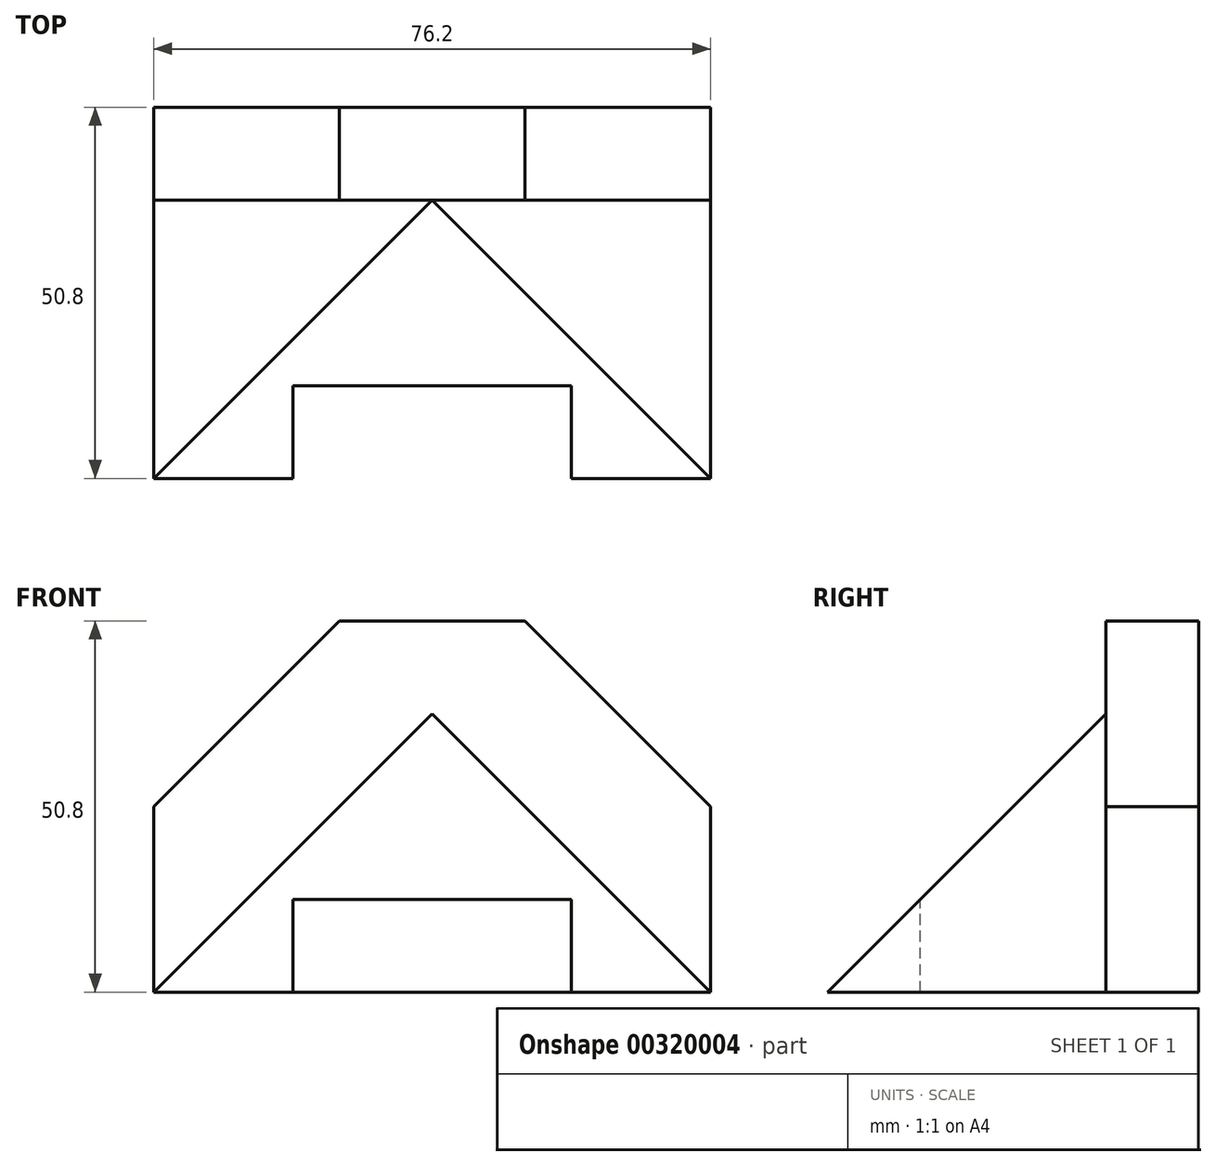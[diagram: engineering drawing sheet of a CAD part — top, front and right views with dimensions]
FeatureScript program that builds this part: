
annotation { "Feature Type Name" : "Feature", "Feature Type Description" : "" }
export const myFeature = defineFeature(function(context is Context, id is Id, definition is map)
    precondition{}
    {
        {
            var Q0;
            Q0=qCreatedBy(makeId("Front.planeOp"),FACE);
            var sketch = newSketch(context, id + "F0", { "sketchPlane" : qUnion([Q0])});
            skLineSegment(sketch, "E0.bottom", {"start": v(0, 0) * mm, "end": v(76.2, 0) * mm});
            skLineSegment(sketch, "E0.top", {"start": v(0, 50.8) * mm, "end": v(76.2, 50.8) * mm});
            skLineSegment(sketch, "E0.left", {"start": v(0, 0) * mm, "end": v(0, 50.8) * mm});
            skLineSegment(sketch, "E0.right", {"start": v(76.2, 0) * mm, "end": v(76.2, 50.8) * mm});
            skSolve(sketch);
        }
        {
            var Q0;
            Q0 = qSketchRegion(id + "F0", true);
            extrude(context, id + "F1", {"entities" : qUnion([Q0]), "oppositeDirection" : true, "depth" : 50.8 * mm});
        }
        {
            var Q0;
            Q0=makeQuery(id+"F1.opExtrude","CAP_FACE",FACE,{"disambiguationData":[OSD([sQuery(id+"F0.wireOp",EDGE,"E0.bottom"),sQuery(id+"F0.wireOp",EDGE,"E0.top"),sQuery(id+"F0.wireOp",EDGE,"E0.left"),sQuery(id+"F0.wireOp",EDGE,"E0.right")])],"isStart":true});
            var sketch = newSketch(context, id + "F2", { "sketchPlane" : qUnion([Q0])});
            skLineSegment(sketch, "E1.bottom", {"start": v(19.05, 0) * mm, "end": v(57.15, 0) * mm});
            skLineSegment(sketch, "E1.top", {"start": v(19.05, 12.7) * mm, "end": v(57.15, 12.7) * mm});
            skLineSegment(sketch, "E1.left", {"start": v(19.05, 0) * mm, "end": v(19.05, 12.7) * mm});
            skLineSegment(sketch, "E1.right", {"start": v(57.15, 0) * mm, "end": v(57.15, 12.7) * mm});
            skPoint(sketch, "E2.start.orphan", {"position": v(38.1, 0) * mm});
            skSolve(sketch);
        }
        {
            var Q0;
            Q0 = qSketchRegion(id + "F2", true);
            extrude(context, id + "F3", {"entities" : qUnion([Q0]), "operationType" : NewBodyOperationType.REMOVE, "oppositeDirection" : true, "depth" : 12.7 * mm});
        }
        {
            var Q0;
            Q0=makeQuery(id+"F1.opExtrude","SWEPT_FACE",FACE,{"disambiguationData":[OSD([sQuery(id+"F0.wireOp",EDGE,"E0.right")])]});
            var sketch = newSketch(context, id + "F4", { "sketchPlane" : qUnion([Q0])});
            skLineSegment(sketch, "E3", {"start": v(0, 0) * mm, "end": v(0, 50.8) * mm});
            skLineSegment(sketch, "E4", {"start": v(0, 50.8) * mm, "end": v(38.1, 50.8) * mm});
            skLineSegment(sketch, "E5", {"start": v(38.1, 50.8) * mm, "end": v(38.1, 38.1) * mm});
            skLineSegment(sketch, "E6", {"start": v(38.1, 38.1) * mm, "end": v(0, 0) * mm});
            skSolve(sketch);
        }
        {
            var Q0;
            Q0 = qSketchRegion(id + "F4", true);
            extrude(context, id + "F5", {"entities" : qUnion([Q0]), "operationType" : NewBodyOperationType.REMOVE, "endBound" : BoundingType.THROUGH_ALL, "oppositeDirection" : true, "depth" : 25.4 * mm});
        }
        {
            var Q0;
            Q0=makeQuery(id+"F1.opExtrude","CAP_FACE",FACE,{"disambiguationData":[OSD([sQuery(id+"F0.wireOp",EDGE,"E0.bottom"),sQuery(id+"F0.wireOp",EDGE,"E0.top"),sQuery(id+"F0.wireOp",EDGE,"E0.left"),sQuery(id+"F0.wireOp",EDGE,"E0.right")])],"isStart":false});
            var sketch = newSketch(context, id + "F6", { "sketchPlane" : qUnion([Q0])});
            skLineSegment(sketch, "E7", {"start": v(-25.4, 50.8) * mm, "end": v(0, 50.8) * mm});
            skLineSegment(sketch, "E8", {"start": v(0, 50.8) * mm, "end": v(0, 25.4) * mm});
            skLineSegment(sketch, "E9", {"start": v(0, 25.4) * mm, "end": v(-25.4, 50.8) * mm});
            skLineSegment(sketch, "E10", {"start": v(-50.8, 50.8) * mm, "end": v(-76.2, 50.8) * mm});
            skLineSegment(sketch, "E11", {"start": v(-76.2, 50.8) * mm, "end": v(-76.2, 25.4) * mm});
            skLineSegment(sketch, "E12", {"start": v(-76.2, 25.4) * mm, "end": v(-50.8, 50.8) * mm});
            skSolve(sketch);
        }
        {
            var Q0;
            Q0 = qSketchRegion(id + "F6", true);
            extrude(context, id + "F7", {"entities" : qUnion([Q0]), "operationType" : NewBodyOperationType.REMOVE, "endBound" : BoundingType.THROUGH_ALL, "oppositeDirection" : true, "depth" : 25.4 * mm});
        }
        {
            var Q0;
            Q0=qCreatedBy(makeId("Front.planeOp"),FACE);
            cPlane(context, id + "F8", {"entities" : qUnion([Q0]), "cplaneType" : CPlaneType.OFFSET, "offset" : 38.1 * mm, "oppositeDirection" : true, "width" : 152.4 * mm, "height" : 152.4 * mm});
        }
        {
            var Q0;
            Q0=qCreatedBy(id+"F8.planeOp",FACE);
            var sketch = newSketch(context, id + "F9", { "sketchPlane" : qUnion([Q0])});
            skLineSegment(sketch, "E13.0", {"start": v(12.7, 38.1) * mm, "end": v(63.5, 38.1) * mm});
            skPoint(sketch, "E14.0", {"position": v(76.2, 0) * mm});
            skPoint(sketch, "E15.0", {"position": v(0, 0) * mm});
            skLineSegment(sketch, "E16", {"start": v(38.1, 38.1) * mm, "end": v(76.2, 0) * mm});
            skLineSegment(sketch, "E17.0", {"start": v(63.5, 38.1) * mm, "end": v(76.2, 25.4) * mm});
            skLineSegment(sketch, "E18.0", {"start": v(76.2, 25.4) * mm, "end": v(76.2, 0) * mm});
            skLineSegment(sketch, "E19.0", {"start": v(12.7, 38.1) * mm, "end": v(0, 25.4) * mm});
            skLineSegment(sketch, "E20.0", {"start": v(0, 25.4) * mm, "end": v(0, 0) * mm});
            skLineSegment(sketch, "E21", {"start": v(38.1, 38.1) * mm, "end": v(0, 0) * mm});
            skSolve(sketch);
        }
        {
            var Q0;
            Q0 = qSketchRegion(id + "F9", true);
            extrude(context, id + "F10", {"entities" : qUnion([Q0]), "operationType" : NewBodyOperationType.REMOVE, "endBound" : BoundingType.THROUGH_ALL, "depth" : 25.4 * mm});
        }
    });
